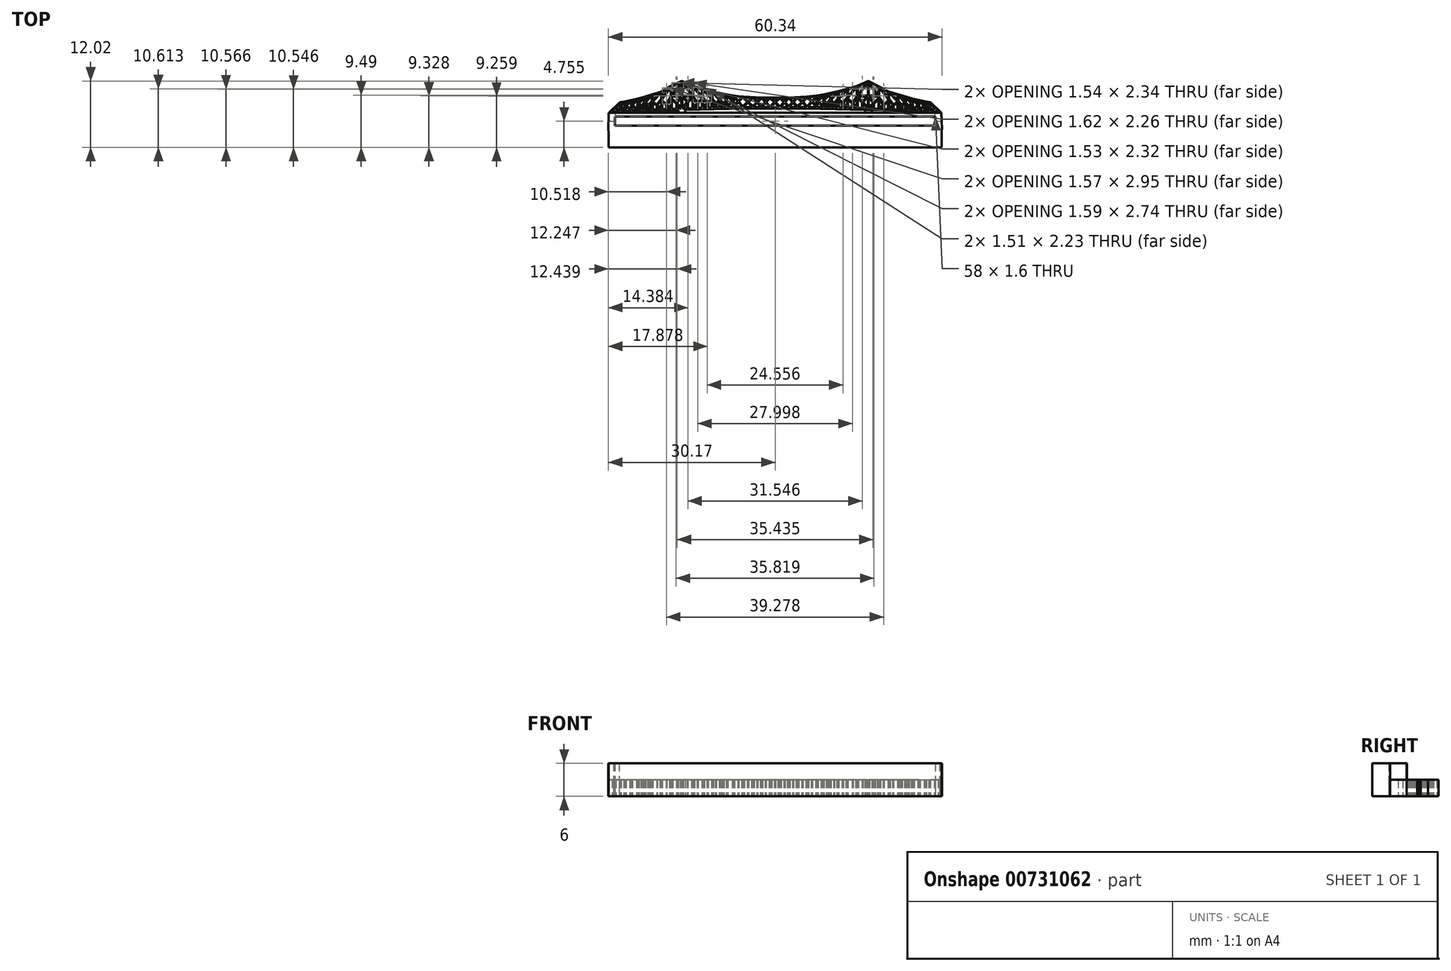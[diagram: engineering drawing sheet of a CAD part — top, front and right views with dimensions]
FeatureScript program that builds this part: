
annotation { "Feature Type Name" : "Feature", "Feature Type Description" : "" }
export const myFeature = defineFeature(function(context is Context, id is Id, definition is map)
    precondition{}
    {
        {
            var Q0;
            Q0=qCreatedBy(makeId("Top.planeOp"),FACE);
            var sketch = newSketch(context, id + "F0", { "sketchPlane" : qUnion([Q0])});
            skLineSegment(sketch, "E0", {"start": v(-17.64, -5.59) * mm, "end": v(-16.17, -5.64) * mm});
            skLineSegment(sketch, "E1", {"start": v(-16.17, -5.64) * mm, "end": v(-16.3, 0.12) * mm});
            skLineSegment(sketch, "E2", {"start": v(-16.3, 0.12) * mm, "end": v(-17.5, 0) * mm});
            skLineSegment(sketch, "E3", {"start": v(-17.5, 0) * mm, "end": v(-17.64, -5.59) * mm});
            skLineSegment(sketch, "E4", {"start": v(-30.17, -3.73) * mm, "end": v(-28.85, -3.82) * mm});
            skLineSegment(sketch, "E5", {"start": v(-28.85, -3.82) * mm, "end": v(-28.91, -0.44) * mm});
            skLineSegment(sketch, "E6", {"start": v(-28.91, -0.44) * mm, "end": v(-30.11, -0.52) * mm});
            skLineSegment(sketch, "E7", {"start": v(-30.11, -0.52) * mm, "end": v(-30.17, -3.73) * mm});
            skLineSegment(sketch, "E8", {"start": v(17.53, -3.47) * mm, "end": v(16.2, -3.47) * mm});
            skLineSegment(sketch, "E9", {"start": v(16.2, -3.47) * mm, "end": v(16.26, 0.16) * mm});
            skLineSegment(sketch, "E10", {"start": v(16.26, 0.16) * mm, "end": v(17.47, 0.13) * mm});
            skLineSegment(sketch, "E11", {"start": v(17.47, 0.13) * mm, "end": v(17.53, -3.47) * mm});
            skLineSegment(sketch, "E12", {"start": v(28.81, -3.47) * mm, "end": v(30.17, -3.47) * mm});
            skLineSegment(sketch, "E13", {"start": v(30.17, -3.47) * mm, "end": v(30.1, -0.5) * mm});
            skLineSegment(sketch, "E14", {"start": v(30.1, -0.5) * mm, "end": v(28.9, -0.37) * mm});
            skLineSegment(sketch, "E15", {"start": v(28.9, -0.37) * mm, "end": v(28.81, -3.47) * mm});
            skLineSegment(sketch, "E16", {"start": v(-18.7, 2.63) * mm, "end": v(-18.7, 4.23) * mm});
            skLineSegment(sketch, "E17", {"start": v(-18.7, 4.23) * mm, "end": v(-17.15, 4.99) * mm});
            skLineSegment(sketch, "E18", {"start": v(-17.15, 4.99) * mm, "end": v(-18.7, 2.64) * mm});
            skLineSegment(sketch, "E19", {"start": v(-16.6, 5) * mm, "end": v(-14.98, 2.73) * mm});
            skLineSegment(sketch, "E20", {"start": v(-14.98, 2.73) * mm, "end": v(-14.98, 4.26) * mm});
            skLineSegment(sketch, "E21", {"start": v(-14.98, 4.26) * mm, "end": v(-16.6, 5) * mm});
            skLineSegment(sketch, "E22", {"start": v(-16.8, 2.38) * mm, "end": v(-16.8, 0.54) * mm});
            skLineSegment(sketch, "E23", {"start": v(-16.8, 0.54) * mm, "end": v(-15.95, 1.45) * mm});
            skLineSegment(sketch, "E24", {"start": v(-15.95, 1.45) * mm, "end": v(-16.8, 2.38) * mm});
            skLineSegment(sketch, "E25", {"start": v(-16.96, 2.35) * mm, "end": v(-16.96, 0.53) * mm});
            skLineSegment(sketch, "E26", {"start": v(-16.96, 0.53) * mm, "end": v(-17.74, 1.25) * mm});
            skLineSegment(sketch, "E27", {"start": v(-17.74, 1.25) * mm, "end": v(-16.96, 2.35) * mm});
            skLineSegment(sketch, "E28", {"start": v(-18.87, 2.07) * mm, "end": v(-18.87, 0.45) * mm});
            skLineSegment(sketch, "E29", {"start": v(-18.87, 0.45) * mm, "end": v(-19.57, 1) * mm});
            skLineSegment(sketch, "E30", {"start": v(-19.57, 1) * mm, "end": v(-18.87, 2.07) * mm});
            skLineSegment(sketch, "E31", {"start": v(-20.6, 1.8) * mm, "end": v(-20.6, 0.37) * mm});
            skLineSegment(sketch, "E32", {"start": v(-20.6, 0.37) * mm, "end": v(-21.3, 0.92) * mm});
            skLineSegment(sketch, "E33", {"start": v(-21.3, 0.92) * mm, "end": v(-20.6, 1.8) * mm});
            skLineSegment(sketch, "E34", {"start": v(-22.33, 1.4) * mm, "end": v(-22.33, 0.34) * mm});
            skLineSegment(sketch, "E35", {"start": v(-22.33, 0.34) * mm, "end": v(-22.86, 0.88) * mm});
            skLineSegment(sketch, "E36", {"start": v(-22.86, 0.88) * mm, "end": v(-22.33, 1.4) * mm});
            skLineSegment(sketch, "E37", {"start": v(-23.7, 1.14) * mm, "end": v(-23.7, 0.29) * mm});
            skLineSegment(sketch, "E38", {"start": v(-23.7, 0.29) * mm, "end": v(-24.12, 0.71) * mm});
            skLineSegment(sketch, "E39", {"start": v(-24.12, 0.71) * mm, "end": v(-23.7, 1.14) * mm});
            skLineSegment(sketch, "E40", {"start": v(-27.92, 0.89) * mm, "end": v(-27.92, 1.3) * mm});
            skLineSegment(sketch, "E41", {"start": v(-27.92, 1.3) * mm, "end": v(-27.43, 1.37) * mm});
            skLineSegment(sketch, "E42", {"start": v(-27.43, 1.37) * mm, "end": v(-27.92, 0.89) * mm});
            skLineSegment(sketch, "E43", {"start": v(-27.05, 0.87) * mm, "end": v(-27.05, 1.45) * mm});
            skLineSegment(sketch, "E44", {"start": v(-27.05, 1.45) * mm, "end": v(-26.3, 1.61) * mm});
            skLineSegment(sketch, "E45", {"start": v(-26.3, 1.61) * mm, "end": v(-27.05, 0.87) * mm});
            skLineSegment(sketch, "E46", {"start": v(-25.9, 1.7) * mm, "end": v(-25.9, 1.08) * mm});
            skLineSegment(sketch, "E47", {"start": v(-25.9, 1.08) * mm, "end": v(-25.15, 1.84) * mm});
            skLineSegment(sketch, "E48", {"start": v(-25.15, 1.84) * mm, "end": v(-25.9, 1.7) * mm});
            skLineSegment(sketch, "E49", {"start": v(-24.76, 1.92) * mm, "end": v(-24.76, 1.35) * mm});
            skLineSegment(sketch, "E50", {"start": v(-24.76, 1.35) * mm, "end": v(-23.96, 2.16) * mm});
            skLineSegment(sketch, "E51", {"start": v(-23.96, 2.16) * mm, "end": v(-24.76, 1.92) * mm});
            skLineSegment(sketch, "E52", {"start": v(-23.53, 1.57) * mm, "end": v(-23.53, 2.28) * mm});
            skLineSegment(sketch, "E53", {"start": v(-23.53, 2.28) * mm, "end": v(-22.57, 2.58) * mm});
            skLineSegment(sketch, "E54", {"start": v(-22.57, 2.58) * mm, "end": v(-23.53, 1.57) * mm});
            skLineSegment(sketch, "E55", {"start": v(-22.16, 1.82) * mm, "end": v(-22.16, 2.7) * mm});
            skLineSegment(sketch, "E56", {"start": v(-22.16, 2.7) * mm, "end": v(-20.87, 3.11) * mm});
            skLineSegment(sketch, "E57", {"start": v(-20.87, 3.11) * mm, "end": v(-22.16, 1.82) * mm});
            skLineSegment(sketch, "E58", {"start": v(-20.44, 2.3) * mm, "end": v(-20.44, 3.27) * mm});
            skLineSegment(sketch, "E59", {"start": v(-20.44, 3.27) * mm, "end": v(-19.13, 4) * mm});
            skLineSegment(sketch, "E60", {"start": v(-19.13, 4) * mm, "end": v(-20.44, 2.3) * mm});
            skLineSegment(sketch, "E61", {"start": v(-14.8, 2.2) * mm, "end": v(-14.13, 1.26) * mm});
            skLineSegment(sketch, "E62", {"start": v(-14.13, 1.26) * mm, "end": v(-14.8, 0.59) * mm});
            skLineSegment(sketch, "E63", {"start": v(-14.8, 0.59) * mm, "end": v(-14.8, 2.2) * mm});
            skLineSegment(sketch, "E64", {"start": v(-13.05, 2.06) * mm, "end": v(-13.05, 0.7) * mm});
            skLineSegment(sketch, "E65", {"start": v(-13.05, 0.7) * mm, "end": v(-12.37, 1.28) * mm});
            skLineSegment(sketch, "E66", {"start": v(-12.37, 1.28) * mm, "end": v(-13.05, 2.06) * mm});
            skLineSegment(sketch, "E67", {"start": v(-11.35, 1.8) * mm, "end": v(-11.35, 0.71) * mm});
            skLineSegment(sketch, "E68", {"start": v(-11.35, 0.71) * mm, "end": v(-10.81, 1.22) * mm});
            skLineSegment(sketch, "E69", {"start": v(-10.81, 1.22) * mm, "end": v(-11.35, 1.8) * mm});
            skLineSegment(sketch, "E70", {"start": v(-13.22, 2.53) * mm, "end": v(-13.22, 3.75) * mm});
            skLineSegment(sketch, "E71", {"start": v(-13.22, 3.75) * mm, "end": v(-14.6, 4.14) * mm});
            skLineSegment(sketch, "E72", {"start": v(-14.6, 4.14) * mm, "end": v(-13.22, 2.53) * mm});
            skLineSegment(sketch, "E73", {"start": v(-11.53, 2.24) * mm, "end": v(-11.53, 3.25) * mm});
            skLineSegment(sketch, "E74", {"start": v(-11.53, 3.25) * mm, "end": v(-12.82, 3.63) * mm});
            skLineSegment(sketch, "E75", {"start": v(-12.82, 3.63) * mm, "end": v(-11.53, 2.24) * mm});
            skLineSegment(sketch, "E76", {"start": v(-10.12, 2.11) * mm, "end": v(-10.12, 2.95) * mm});
            skLineSegment(sketch, "E77", {"start": v(-10.12, 2.95) * mm, "end": v(-11.14, 3.16) * mm});
            skLineSegment(sketch, "E78", {"start": v(-11.14, 3.16) * mm, "end": v(-10.12, 2.11) * mm});
            skLineSegment(sketch, "E79", {"start": v(-8.9, 2.03) * mm, "end": v(-8.9, 2.7) * mm});
            skLineSegment(sketch, "E80", {"start": v(-8.9, 2.7) * mm, "end": v(-9.73, 2.87) * mm});
            skLineSegment(sketch, "E81", {"start": v(-9.73, 2.87) * mm, "end": v(-8.9, 2.03) * mm});
            skLineSegment(sketch, "E82", {"start": v(-7.66, 1.77) * mm, "end": v(-7.66, 2.51) * mm});
            skLineSegment(sketch, "E83", {"start": v(-7.66, 2.51) * mm, "end": v(-8.52, 2.64) * mm});
            skLineSegment(sketch, "E84", {"start": v(-8.52, 2.64) * mm, "end": v(-7.66, 1.77) * mm});
            skLineSegment(sketch, "E85", {"start": v(-9.95, 1.7) * mm, "end": v(-9.95, 0.75) * mm});
            skLineSegment(sketch, "E86", {"start": v(-9.95, 0.75) * mm, "end": v(-9.48, 1.21) * mm});
            skLineSegment(sketch, "E87", {"start": v(-9.48, 1.21) * mm, "end": v(-9.95, 1.7) * mm});
            skLineSegment(sketch, "E88", {"start": v(-7.5, 0.53) * mm, "end": v(-6.67, 1.4) * mm});
            skLineSegment(sketch, "E89", {"start": v(-6.67, 1.4) * mm, "end": v(-5.94, 0.53) * mm});
            skLineSegment(sketch, "E90", {"start": v(-5.94, 0.53) * mm, "end": v(-7.5, 0.53) * mm});
            skLineSegment(sketch, "E91", {"start": v(-5.77, 0.52) * mm, "end": v(-4.94, 1.36) * mm});
            skLineSegment(sketch, "E92", {"start": v(-4.94, 1.36) * mm, "end": v(-4.14, 0.55) * mm});
            skLineSegment(sketch, "E93", {"start": v(-4.14, 0.55) * mm, "end": v(-5.77, 0.53) * mm});
            skLineSegment(sketch, "E94", {"start": v(-3.97, 0.55) * mm, "end": v(-3.25, 1.3) * mm});
            skLineSegment(sketch, "E95", {"start": v(-3.25, 1.3) * mm, "end": v(-2.58, 0.55) * mm});
            skLineSegment(sketch, "E96", {"start": v(-2.58, 0.55) * mm, "end": v(-3.97, 0.55) * mm});
            skLineSegment(sketch, "E97", {"start": v(-1.7, 1.3) * mm, "end": v(-2.4, 0.55) * mm});
            skLineSegment(sketch, "E98", {"start": v(-2.4, 0.55) * mm, "end": v(-0.98, 0.55) * mm});
            skLineSegment(sketch, "E99", {"start": v(-0.98, 0.55) * mm, "end": v(-1.7, 1.3) * mm});
            skLineSegment(sketch, "E100", {"start": v(-1.7, 1.54) * mm, "end": v(-1.15, 2.1) * mm});
            skLineSegment(sketch, "E101", {"start": v(-1.15, 2.1) * mm, "end": v(-2.24, 2.1) * mm});
            skLineSegment(sketch, "E102", {"start": v(-2.24, 2.1) * mm, "end": v(-1.7, 1.54) * mm});
            skLineSegment(sketch, "E103", {"start": v(-2.72, 2.12) * mm, "end": v(-3.8, 2.18) * mm});
            skLineSegment(sketch, "E104", {"start": v(-3.8, 2.18) * mm, "end": v(-3.25, 1.56) * mm});
            skLineSegment(sketch, "E105", {"start": v(-3.25, 1.56) * mm, "end": v(-2.72, 2.12) * mm});
            skLineSegment(sketch, "E106", {"start": v(-4.3, 2.2) * mm, "end": v(-4.92, 1.6) * mm});
            skLineSegment(sketch, "E107", {"start": v(-4.92, 1.6) * mm, "end": v(-5.59, 2.27) * mm});
            skLineSegment(sketch, "E108", {"start": v(-5.59, 2.27) * mm, "end": v(-4.3, 2.2) * mm});
            skLineSegment(sketch, "E109", {"start": v(-7.33, 2.47) * mm, "end": v(-6.66, 1.67) * mm});
            skLineSegment(sketch, "E110", {"start": v(-6.66, 1.67) * mm, "end": v(-6.07, 2.31) * mm});
            skLineSegment(sketch, "E111", {"start": v(-6.07, 2.31) * mm, "end": v(-7.33, 2.47) * mm});
            skLineSegment(sketch, "E112", {"start": v(18.67, 2.63) * mm, "end": v(18.67, 4.23) * mm});
            skLineSegment(sketch, "E113", {"start": v(18.67, 4.23) * mm, "end": v(17.12, 4.99) * mm});
            skLineSegment(sketch, "E114", {"start": v(17.12, 4.99) * mm, "end": v(18.67, 2.64) * mm});
            skLineSegment(sketch, "E115", {"start": v(16.57, 5) * mm, "end": v(14.95, 2.73) * mm});
            skLineSegment(sketch, "E116", {"start": v(14.95, 2.73) * mm, "end": v(14.95, 4.26) * mm});
            skLineSegment(sketch, "E117", {"start": v(14.95, 4.26) * mm, "end": v(16.57, 5) * mm});
            skLineSegment(sketch, "E118", {"start": v(16.77, 2.38) * mm, "end": v(16.77, 0.54) * mm});
            skLineSegment(sketch, "E119", {"start": v(16.77, 0.54) * mm, "end": v(15.92, 1.45) * mm});
            skLineSegment(sketch, "E120", {"start": v(15.92, 1.45) * mm, "end": v(16.77, 2.38) * mm});
            skLineSegment(sketch, "E121", {"start": v(16.94, 2.35) * mm, "end": v(16.94, 0.53) * mm});
            skLineSegment(sketch, "E122", {"start": v(16.94, 0.53) * mm, "end": v(17.71, 1.25) * mm});
            skLineSegment(sketch, "E123", {"start": v(17.71, 1.25) * mm, "end": v(16.94, 2.35) * mm});
            skLineSegment(sketch, "E124", {"start": v(18.84, 2.07) * mm, "end": v(18.84, 0.45) * mm});
            skLineSegment(sketch, "E125", {"start": v(18.84, 0.45) * mm, "end": v(19.54, 1) * mm});
            skLineSegment(sketch, "E126", {"start": v(19.54, 1) * mm, "end": v(18.84, 2.07) * mm});
            skLineSegment(sketch, "E127", {"start": v(20.58, 1.8) * mm, "end": v(20.58, 0.37) * mm});
            skLineSegment(sketch, "E128", {"start": v(20.58, 0.37) * mm, "end": v(21.26, 0.92) * mm});
            skLineSegment(sketch, "E129", {"start": v(21.26, 0.92) * mm, "end": v(20.58, 1.8) * mm});
            skLineSegment(sketch, "E130", {"start": v(22.3, 1.4) * mm, "end": v(22.3, 0.34) * mm});
            skLineSegment(sketch, "E131", {"start": v(22.3, 0.34) * mm, "end": v(22.84, 0.88) * mm});
            skLineSegment(sketch, "E132", {"start": v(22.84, 0.88) * mm, "end": v(22.3, 1.4) * mm});
            skLineSegment(sketch, "E133", {"start": v(23.68, 1.14) * mm, "end": v(23.68, 0.29) * mm});
            skLineSegment(sketch, "E134", {"start": v(23.68, 0.29) * mm, "end": v(24.1, 0.71) * mm});
            skLineSegment(sketch, "E135", {"start": v(24.1, 0.71) * mm, "end": v(23.68, 1.14) * mm});
            skLineSegment(sketch, "E136", {"start": v(27.9, 0.89) * mm, "end": v(27.9, 1.3) * mm});
            skLineSegment(sketch, "E137", {"start": v(27.9, 1.3) * mm, "end": v(27.4, 1.37) * mm});
            skLineSegment(sketch, "E138", {"start": v(27.4, 1.37) * mm, "end": v(27.9, 0.89) * mm});
            skLineSegment(sketch, "E139", {"start": v(27.02, 0.87) * mm, "end": v(27.02, 1.45) * mm});
            skLineSegment(sketch, "E140", {"start": v(27.02, 1.45) * mm, "end": v(26.28, 1.61) * mm});
            skLineSegment(sketch, "E141", {"start": v(26.28, 1.61) * mm, "end": v(27.02, 0.87) * mm});
            skLineSegment(sketch, "E142", {"start": v(25.88, 1.7) * mm, "end": v(25.88, 1.08) * mm});
            skLineSegment(sketch, "E143", {"start": v(25.88, 1.08) * mm, "end": v(25.12, 1.84) * mm});
            skLineSegment(sketch, "E144", {"start": v(25.12, 1.84) * mm, "end": v(25.88, 1.7) * mm});
            skLineSegment(sketch, "E145", {"start": v(24.73, 1.92) * mm, "end": v(24.73, 1.35) * mm});
            skLineSegment(sketch, "E146", {"start": v(24.73, 1.35) * mm, "end": v(23.93, 2.16) * mm});
            skLineSegment(sketch, "E147", {"start": v(23.93, 2.16) * mm, "end": v(24.73, 1.92) * mm});
            skLineSegment(sketch, "E148", {"start": v(23.5, 1.57) * mm, "end": v(23.5, 2.28) * mm});
            skLineSegment(sketch, "E149", {"start": v(23.5, 2.28) * mm, "end": v(22.55, 2.58) * mm});
            skLineSegment(sketch, "E150", {"start": v(22.55, 2.58) * mm, "end": v(23.5, 1.57) * mm});
            skLineSegment(sketch, "E151", {"start": v(22.13, 1.82) * mm, "end": v(22.13, 2.7) * mm});
            skLineSegment(sketch, "E152", {"start": v(22.13, 2.7) * mm, "end": v(20.85, 3.11) * mm});
            skLineSegment(sketch, "E153", {"start": v(20.85, 3.11) * mm, "end": v(22.13, 1.82) * mm});
            skLineSegment(sketch, "E154", {"start": v(20.41, 2.3) * mm, "end": v(20.41, 3.27) * mm});
            skLineSegment(sketch, "E155", {"start": v(20.41, 3.27) * mm, "end": v(19.1, 4) * mm});
            skLineSegment(sketch, "E156", {"start": v(19.1, 4) * mm, "end": v(20.41, 2.3) * mm});
            skLineSegment(sketch, "E157", {"start": v(14.78, 2.2) * mm, "end": v(14.1, 1.26) * mm});
            skLineSegment(sketch, "E158", {"start": v(14.1, 1.26) * mm, "end": v(14.78, 0.59) * mm});
            skLineSegment(sketch, "E159", {"start": v(14.78, 0.59) * mm, "end": v(14.78, 2.2) * mm});
            skLineSegment(sketch, "E160", {"start": v(13.02, 2.06) * mm, "end": v(13.02, 0.7) * mm});
            skLineSegment(sketch, "E161", {"start": v(13.02, 0.7) * mm, "end": v(12.35, 1.28) * mm});
            skLineSegment(sketch, "E162", {"start": v(12.35, 1.28) * mm, "end": v(13.02, 2.06) * mm});
            skLineSegment(sketch, "E163", {"start": v(11.33, 1.8) * mm, "end": v(11.33, 0.71) * mm});
            skLineSegment(sketch, "E164", {"start": v(11.33, 0.71) * mm, "end": v(10.78, 1.22) * mm});
            skLineSegment(sketch, "E165", {"start": v(10.78, 1.22) * mm, "end": v(11.33, 1.8) * mm});
            skLineSegment(sketch, "E166", {"start": v(13.2, 2.53) * mm, "end": v(13.2, 3.75) * mm});
            skLineSegment(sketch, "E167", {"start": v(13.2, 3.75) * mm, "end": v(14.58, 4.14) * mm});
            skLineSegment(sketch, "E168", {"start": v(14.58, 4.14) * mm, "end": v(13.2, 2.53) * mm});
            skLineSegment(sketch, "E169", {"start": v(11.5, 2.24) * mm, "end": v(11.5, 3.25) * mm});
            skLineSegment(sketch, "E170", {"start": v(11.5, 3.25) * mm, "end": v(12.8, 3.63) * mm});
            skLineSegment(sketch, "E171", {"start": v(12.8, 3.63) * mm, "end": v(11.5, 2.24) * mm});
            skLineSegment(sketch, "E172", {"start": v(10.1, 2.11) * mm, "end": v(10.1, 2.95) * mm});
            skLineSegment(sketch, "E173", {"start": v(10.1, 2.95) * mm, "end": v(11.11, 3.16) * mm});
            skLineSegment(sketch, "E174", {"start": v(11.11, 3.16) * mm, "end": v(10.1, 2.11) * mm});
            skLineSegment(sketch, "E175", {"start": v(8.87, 2.03) * mm, "end": v(8.87, 2.7) * mm});
            skLineSegment(sketch, "E176", {"start": v(8.87, 2.7) * mm, "end": v(9.7, 2.87) * mm});
            skLineSegment(sketch, "E177", {"start": v(9.7, 2.87) * mm, "end": v(8.87, 2.03) * mm});
            skLineSegment(sketch, "E178", {"start": v(7.64, 1.77) * mm, "end": v(7.64, 2.51) * mm});
            skLineSegment(sketch, "E179", {"start": v(7.64, 2.51) * mm, "end": v(8.5, 2.64) * mm});
            skLineSegment(sketch, "E180", {"start": v(8.5, 2.64) * mm, "end": v(7.64, 1.77) * mm});
            skLineSegment(sketch, "E181", {"start": v(9.92, 1.7) * mm, "end": v(9.92, 0.75) * mm});
            skLineSegment(sketch, "E182", {"start": v(9.92, 0.75) * mm, "end": v(9.45, 1.21) * mm});
            skLineSegment(sketch, "E183", {"start": v(9.45, 1.21) * mm, "end": v(9.92, 1.7) * mm});
            skLineSegment(sketch, "E184", {"start": v(7.46, 0.53) * mm, "end": v(6.64, 1.4) * mm});
            skLineSegment(sketch, "E185", {"start": v(6.64, 1.4) * mm, "end": v(5.91, 0.53) * mm});
            skLineSegment(sketch, "E186", {"start": v(5.91, 0.53) * mm, "end": v(7.46, 0.53) * mm});
            skLineSegment(sketch, "E187", {"start": v(5.74, 0.53) * mm, "end": v(4.9, 1.36) * mm});
            skLineSegment(sketch, "E188", {"start": v(4.9, 1.36) * mm, "end": v(4.11, 0.55) * mm});
            skLineSegment(sketch, "E189", {"start": v(4.11, 0.55) * mm, "end": v(5.74, 0.53) * mm});
            skLineSegment(sketch, "E190", {"start": v(3.94, 0.55) * mm, "end": v(3.23, 1.3) * mm});
            skLineSegment(sketch, "E191", {"start": v(3.23, 1.3) * mm, "end": v(2.55, 0.55) * mm});
            skLineSegment(sketch, "E192", {"start": v(2.55, 0.55) * mm, "end": v(3.94, 0.55) * mm});
            skLineSegment(sketch, "E193", {"start": v(1.67, 1.3) * mm, "end": v(2.38, 0.55) * mm});
            skLineSegment(sketch, "E194", {"start": v(2.38, 0.55) * mm, "end": v(0.95, 0.55) * mm});
            skLineSegment(sketch, "E195", {"start": v(0.95, 0.55) * mm, "end": v(1.67, 1.3) * mm});
            skLineSegment(sketch, "E196", {"start": v(1.67, 1.54) * mm, "end": v(1.12, 2.1) * mm});
            skLineSegment(sketch, "E197", {"start": v(1.12, 2.1) * mm, "end": v(2.21, 2.1) * mm});
            skLineSegment(sketch, "E198", {"start": v(2.21, 2.1) * mm, "end": v(1.67, 1.54) * mm});
            skLineSegment(sketch, "E199", {"start": v(2.7, 2.12) * mm, "end": v(3.78, 2.18) * mm});
            skLineSegment(sketch, "E200", {"start": v(3.78, 2.18) * mm, "end": v(3.22, 1.56) * mm});
            skLineSegment(sketch, "E201", {"start": v(3.22, 1.56) * mm, "end": v(2.7, 2.12) * mm});
            skLineSegment(sketch, "E202", {"start": v(4.27, 2.2) * mm, "end": v(4.9, 1.6) * mm});
            skLineSegment(sketch, "E203", {"start": v(4.9, 1.6) * mm, "end": v(5.56, 2.27) * mm});
            skLineSegment(sketch, "E204", {"start": v(5.56, 2.27) * mm, "end": v(4.27, 2.2) * mm});
            skLineSegment(sketch, "E205", {"start": v(7.3, 2.47) * mm, "end": v(6.64, 1.67) * mm});
            skLineSegment(sketch, "E206", {"start": v(6.64, 1.67) * mm, "end": v(6.04, 2.31) * mm});
            skLineSegment(sketch, "E207", {"start": v(6.04, 2.31) * mm, "end": v(7.3, 2.47) * mm});
            skLineSegment(sketch, "E208", {"start": v(-0.05, 1.29) * mm, "end": v(-0.76, 0.55) * mm});
            skLineSegment(sketch, "E209", {"start": v(-0.76, 0.55) * mm, "end": v(0.67, 0.54) * mm});
            skLineSegment(sketch, "E210", {"start": v(0.67, 0.54) * mm, "end": v(-0.05, 1.29) * mm});
            skLineSegment(sketch, "E211", {"start": v(-0.05, 1.53) * mm, "end": v(0.5, 2.1) * mm});
            skLineSegment(sketch, "E212", {"start": v(0.5, 2.1) * mm, "end": v(-0.6, 2.1) * mm});
            skLineSegment(sketch, "E213", {"start": v(-0.6, 2.1) * mm, "end": v(-0.05, 1.53) * mm});
            skLineSegment(sketch, "E214", {"start": v(18.84, 4.05) * mm, "end": v(20.41, 2.02) * mm});
            skLineSegment(sketch, "E215", {"start": v(20.41, 2.02) * mm, "end": v(20.41, 1.7) * mm});
            skLineSegment(sketch, "E216", {"start": v(20.41, 1.7) * mm, "end": v(19.71, 1.1) * mm});
            skLineSegment(sketch, "E217", {"start": v(19.71, 1.1) * mm, "end": v(18.84, 2.38) * mm});
            skLineSegment(sketch, "E218", {"start": v(18.84, 2.38) * mm, "end": v(18.84, 4.05) * mm});
            skLineSegment(sketch, "E219", {"start": v(16.94, 4.96) * mm, "end": v(16.94, 2.64) * mm});
            skLineSegment(sketch, "E220", {"start": v(16.94, 2.64) * mm, "end": v(18.47, 2.63) * mm});
            skLineSegment(sketch, "E221", {"start": v(18.47, 2.63) * mm, "end": v(16.94, 4.96) * mm});
            skLineSegment(sketch, "E222", {"start": v(17.05, 2.48) * mm, "end": v(18.58, 2.46) * mm});
            skLineSegment(sketch, "E223", {"start": v(18.58, 2.46) * mm, "end": v(18.67, 2.33) * mm});
            skLineSegment(sketch, "E224", {"start": v(18.67, 2.33) * mm, "end": v(18.71, 2.19) * mm});
            skLineSegment(sketch, "E225", {"start": v(18.71, 2.19) * mm, "end": v(17.84, 1.37) * mm});
            skLineSegment(sketch, "E226", {"start": v(17.84, 1.37) * mm, "end": v(17.05, 2.48) * mm});
            skLineSegment(sketch, "E227", {"start": v(18.67, 0.23) * mm, "end": v(18.67, 1.91) * mm});
            skLineSegment(sketch, "E228", {"start": v(18.67, 1.91) * mm, "end": v(17.88, 1.17) * mm});
            skLineSegment(sketch, "E229", {"start": v(17.88, 1.17) * mm, "end": v(17.88, 0.27) * mm});
            skLineSegment(sketch, "E230", {"start": v(17.88, 0.27) * mm, "end": v(18.67, 0.23) * mm});
            skLineSegment(sketch, "E231", {"start": v(20.41, 0.15) * mm, "end": v(20.41, 1.47) * mm});
            skLineSegment(sketch, "E232", {"start": v(20.41, 1.47) * mm, "end": v(19.71, 0.92) * mm});
            skLineSegment(sketch, "E233", {"start": v(19.71, 0.92) * mm, "end": v(19.71, 0.2) * mm});
            skLineSegment(sketch, "E234", {"start": v(19.71, 0.2) * mm, "end": v(20.41, 0.15) * mm});
            skLineSegment(sketch, "E235", {"start": v(19.54, 0.78) * mm, "end": v(19.54, 0.2) * mm});
            skLineSegment(sketch, "E236", {"start": v(19.54, 0.2) * mm, "end": v(18.84, 0.23) * mm});
            skLineSegment(sketch, "E237", {"start": v(18.84, 0.23) * mm, "end": v(19.54, 0.78) * mm});
            skLineSegment(sketch, "E238", {"start": v(20.58, 3.13) * mm, "end": v(22.12, 1.6) * mm});
            skLineSegment(sketch, "E239", {"start": v(22.12, 1.6) * mm, "end": v(21.4, 1.02) * mm});
            skLineSegment(sketch, "E240", {"start": v(21.4, 1.02) * mm, "end": v(20.58, 2.08) * mm});
            skLineSegment(sketch, "E241", {"start": v(20.58, 2.08) * mm, "end": v(20.58, 3.13) * mm});
            skLineSegment(sketch, "E242", {"start": v(22.13, 1.39) * mm, "end": v(22.13, 0.1) * mm});
            skLineSegment(sketch, "E243", {"start": v(22.13, 0.1) * mm, "end": v(21.44, 0.1) * mm});
            skLineSegment(sketch, "E244", {"start": v(21.44, 0.1) * mm, "end": v(21.44, 0.83) * mm});
            skLineSegment(sketch, "E245", {"start": v(21.44, 0.83) * mm, "end": v(22.13, 1.39) * mm});
            skLineSegment(sketch, "E246", {"start": v(21.27, 0.7) * mm, "end": v(21.27, 0.1) * mm});
            skLineSegment(sketch, "E247", {"start": v(21.27, 0.1) * mm, "end": v(20.58, 0.15) * mm});
            skLineSegment(sketch, "E248", {"start": v(20.58, 0.15) * mm, "end": v(21.27, 0.7) * mm});
            skLineSegment(sketch, "E249", {"start": v(17.7, 1.01) * mm, "end": v(17.7, 0.27) * mm});
            skLineSegment(sketch, "E250", {"start": v(17.7, 0.27) * mm, "end": v(16.94, 0.3) * mm});
            skLineSegment(sketch, "E251", {"start": v(16.94, 0.3) * mm, "end": v(17.7, 1.01) * mm});
            skLineSegment(sketch, "E252", {"start": v(26.05, 1.6) * mm, "end": v(26.92, 0.73) * mm});
            skLineSegment(sketch, "E253", {"start": v(26.92, 0.73) * mm, "end": v(26.05, 0.16) * mm});
            skLineSegment(sketch, "E254", {"start": v(26.05, 0.16) * mm, "end": v(26.05, 1.6) * mm});
            skLineSegment(sketch, "E255", {"start": v(24.9, 1.81) * mm, "end": v(25.79, 0.93) * mm});
            skLineSegment(sketch, "E256", {"start": v(25.79, 0.93) * mm, "end": v(24.9, 0.21) * mm});
            skLineSegment(sketch, "E257", {"start": v(24.9, 0.21) * mm, "end": v(24.9, 1.81) * mm});
            skLineSegment(sketch, "E258", {"start": v(23.68, 2.17) * mm, "end": v(24.6, 1.24) * mm});
            skLineSegment(sketch, "E259", {"start": v(24.6, 1.24) * mm, "end": v(24.21, 0.83) * mm});
            skLineSegment(sketch, "E260", {"start": v(24.21, 0.83) * mm, "end": v(23.68, 1.4) * mm});
            skLineSegment(sketch, "E261", {"start": v(23.68, 1.4) * mm, "end": v(23.68, 2.17) * mm});
            skLineSegment(sketch, "E262", {"start": v(23.5, 1.32) * mm, "end": v(23.5, 0.04) * mm});
            skLineSegment(sketch, "E263", {"start": v(23.5, 0.04) * mm, "end": v(23.03, 0.07) * mm});
            skLineSegment(sketch, "E264", {"start": v(23.03, 0.07) * mm, "end": v(23.03, 0.83) * mm});
            skLineSegment(sketch, "E265", {"start": v(23.03, 0.83) * mm, "end": v(23.5, 1.32) * mm});
            skLineSegment(sketch, "E266", {"start": v(23.39, 1.44) * mm, "end": v(22.96, 1) * mm});
            skLineSegment(sketch, "E267", {"start": v(22.96, 1) * mm, "end": v(22.3, 1.65) * mm});
            skLineSegment(sketch, "E268", {"start": v(22.3, 1.65) * mm, "end": v(22.3, 2.58) * mm});
            skLineSegment(sketch, "E269", {"start": v(22.3, 2.58) * mm, "end": v(23.39, 1.44) * mm});
            skLineSegment(sketch, "E270", {"start": v(22.86, 0.66) * mm, "end": v(22.86, 0.07) * mm});
            skLineSegment(sketch, "E271", {"start": v(22.86, 0.07) * mm, "end": v(22.3, 0.1) * mm});
            skLineSegment(sketch, "E272", {"start": v(22.3, 0.1) * mm, "end": v(22.86, 0.66) * mm});
            skLineSegment(sketch, "E273", {"start": v(24.73, -0.01) * mm, "end": v(24.73, 1.12) * mm});
            skLineSegment(sketch, "E274", {"start": v(24.73, 1.12) * mm, "end": v(24.27, 0.65) * mm});
            skLineSegment(sketch, "E275", {"start": v(24.27, 0.65) * mm, "end": v(24.27, 0.01) * mm});
            skLineSegment(sketch, "E276", {"start": v(24.27, 0.01) * mm, "end": v(24.73, -0.01) * mm});
            skLineSegment(sketch, "E277", {"start": v(24.1, 0.47) * mm, "end": v(24.1, 0.01) * mm});
            skLineSegment(sketch, "E278", {"start": v(24.1, 0.01) * mm, "end": v(23.68, 0.04) * mm});
            skLineSegment(sketch, "E279", {"start": v(23.68, 0.04) * mm, "end": v(24.1, 0.47) * mm});
            skLineSegment(sketch, "E280", {"start": v(25.88, 0.78) * mm, "end": v(25.88, -0.04) * mm});
            skLineSegment(sketch, "E281", {"start": v(25.88, -0.04) * mm, "end": v(24.9, -0.01) * mm});
            skLineSegment(sketch, "E282", {"start": v(24.9, -0.01) * mm, "end": v(25.88, 0.78) * mm});
            skLineSegment(sketch, "E283", {"start": v(27.02, 0.6) * mm, "end": v(27.02, -0.14) * mm});
            skLineSegment(sketch, "E284", {"start": v(27.02, -0.14) * mm, "end": v(26.05, -0.04) * mm});
            skLineSegment(sketch, "E285", {"start": v(26.05, -0.04) * mm, "end": v(27.02, 0.6) * mm});
            skLineSegment(sketch, "E286", {"start": v(27.2, 1.34) * mm, "end": v(27.81, 0.72) * mm});
            skLineSegment(sketch, "E287", {"start": v(27.81, 0.72) * mm, "end": v(27.2, 0.1) * mm});
            skLineSegment(sketch, "E288", {"start": v(27.2, 0.1) * mm, "end": v(27.2, 1.34) * mm});
            skLineSegment(sketch, "E289", {"start": v(27.9, 0.56) * mm, "end": v(27.9, -0.17) * mm});
            skLineSegment(sketch, "E290", {"start": v(27.9, -0.17) * mm, "end": v(27.2, -0.14) * mm});
            skLineSegment(sketch, "E291", {"start": v(27.2, -0.14) * mm, "end": v(27.9, 0.56) * mm});
            skLineSegment(sketch, "E292", {"start": v(28.06, 0.03) * mm, "end": v(28.06, 1.2) * mm});
            skLineSegment(sketch, "E293", {"start": v(28.06, 1.2) * mm, "end": v(28.8, 0.45) * mm});
            skLineSegment(sketch, "E294", {"start": v(28.8, 0.45) * mm, "end": v(28.06, 0.03) * mm});
            skLineSegment(sketch, "E295", {"start": v(28.93, 0.33) * mm, "end": v(29.5, -0.24) * mm});
            skLineSegment(sketch, "E296", {"start": v(29.5, -0.24) * mm, "end": v(28.06, -0.17) * mm});
            skLineSegment(sketch, "E297", {"start": v(28.06, -0.17) * mm, "end": v(28.93, 0.33) * mm});
            skLineSegment(sketch, "E298", {"start": v(6.53, 1.54) * mm, "end": v(5.83, 2.29) * mm});
            skLineSegment(sketch, "E299", {"start": v(5.83, 2.29) * mm, "end": v(5.02, 1.47) * mm});
            skLineSegment(sketch, "E300", {"start": v(5.02, 1.47) * mm, "end": v(5.82, 0.69) * mm});
            skLineSegment(sketch, "E301", {"start": v(5.82, 0.69) * mm, "end": v(6.53, 1.54) * mm});
            skLineSegment(sketch, "E302", {"start": v(4.78, 1.47) * mm, "end": v(4.04, 2.2) * mm});
            skLineSegment(sketch, "E303", {"start": v(4.04, 2.2) * mm, "end": v(3.34, 1.44) * mm});
            skLineSegment(sketch, "E304", {"start": v(3.34, 1.44) * mm, "end": v(4.03, 0.71) * mm});
            skLineSegment(sketch, "E305", {"start": v(4.03, 0.71) * mm, "end": v(4.78, 1.47) * mm});
            skLineSegment(sketch, "E306", {"start": v(2.45, 2.1) * mm, "end": v(3.1, 1.43) * mm});
            skLineSegment(sketch, "E307", {"start": v(3.1, 1.43) * mm, "end": v(2.46, 0.7) * mm});
            skLineSegment(sketch, "E308", {"start": v(2.46, 0.7) * mm, "end": v(1.78, 1.41) * mm});
            skLineSegment(sketch, "E309", {"start": v(1.78, 1.41) * mm, "end": v(2.45, 2.1) * mm});
            skLineSegment(sketch, "E310", {"start": v(0.83, 2.16) * mm, "end": v(1.54, 1.42) * mm});
            skLineSegment(sketch, "E311", {"start": v(1.54, 1.42) * mm, "end": v(0.83, 0.68) * mm});
            skLineSegment(sketch, "E312", {"start": v(0.83, 0.68) * mm, "end": v(0.07, 1.42) * mm});
            skLineSegment(sketch, "E313", {"start": v(0.08, 1.41) * mm, "end": v(0.83, 2.16) * mm});
            skLineSegment(sketch, "E314", {"start": v(-6.55, 1.54) * mm, "end": v(-5.86, 2.29) * mm});
            skLineSegment(sketch, "E315", {"start": v(-5.86, 2.29) * mm, "end": v(-5.04, 1.47) * mm});
            skLineSegment(sketch, "E316", {"start": v(-5.04, 1.47) * mm, "end": v(-5.85, 0.69) * mm});
            skLineSegment(sketch, "E317", {"start": v(-5.85, 0.69) * mm, "end": v(-6.55, 1.54) * mm});
            skLineSegment(sketch, "E318", {"start": v(-4.8, 1.47) * mm, "end": v(-4.06, 2.2) * mm});
            skLineSegment(sketch, "E319", {"start": v(-4.06, 2.2) * mm, "end": v(-3.37, 1.44) * mm});
            skLineSegment(sketch, "E320", {"start": v(-3.37, 1.44) * mm, "end": v(-4.06, 0.71) * mm});
            skLineSegment(sketch, "E321", {"start": v(-4.06, 0.71) * mm, "end": v(-4.8, 1.47) * mm});
            skLineSegment(sketch, "E322", {"start": v(-2.48, 2.1) * mm, "end": v(-3.14, 1.43) * mm});
            skLineSegment(sketch, "E323", {"start": v(-3.14, 1.43) * mm, "end": v(-2.49, 0.7) * mm});
            skLineSegment(sketch, "E324", {"start": v(-2.49, 0.7) * mm, "end": v(-1.81, 1.41) * mm});
            skLineSegment(sketch, "E325", {"start": v(-1.81, 1.41) * mm, "end": v(-2.48, 2.1) * mm});
            skLineSegment(sketch, "E326", {"start": v(-0.93, 2.15) * mm, "end": v(-1.64, 1.41) * mm});
            skLineSegment(sketch, "E327", {"start": v(-1.64, 1.41) * mm, "end": v(-0.93, 0.67) * mm});
            skLineSegment(sketch, "E328", {"start": v(-0.93, 0.67) * mm, "end": v(-0.17, 1.41) * mm});
            skLineSegment(sketch, "E329", {"start": v(-0.17, 1.4) * mm, "end": v(-0.93, 2.15) * mm});
            skLineSegment(sketch, "E330", {"start": v(16.77, 4.97) * mm, "end": v(16.77, 2.63) * mm});
            skLineSegment(sketch, "E331", {"start": v(16.77, 2.63) * mm, "end": v(15.1, 2.65) * mm});
            skLineSegment(sketch, "E332", {"start": v(15.1, 2.65) * mm, "end": v(16.77, 4.97) * mm});
            skLineSegment(sketch, "E333", {"start": v(16.61, 2.46) * mm, "end": v(15.8, 1.57) * mm});
            skLineSegment(sketch, "E334", {"start": v(15.8, 1.57) * mm, "end": v(14.97, 2.46) * mm});
            skLineSegment(sketch, "E335", {"start": v(14.97, 2.46) * mm, "end": v(14.98, 2.48) * mm});
            skLineSegment(sketch, "E336", {"start": v(14.98, 2.48) * mm, "end": v(16.61, 2.46) * mm});
            skLineSegment(sketch, "E337", {"start": v(14.78, 4.1) * mm, "end": v(14.78, 2.5) * mm});
            skLineSegment(sketch, "E338", {"start": v(14.78, 2.5) * mm, "end": v(13.98, 1.37) * mm});
            skLineSegment(sketch, "E339", {"start": v(13.98, 1.37) * mm, "end": v(13.2, 2.14) * mm});
            skLineSegment(sketch, "E340", {"start": v(13.2, 2.14) * mm, "end": v(13.2, 2.26) * mm});
            skLineSegment(sketch, "E341", {"start": v(13.2, 2.26) * mm, "end": v(14.78, 4.1) * mm});
            skLineSegment(sketch, "E342", {"start": v(13.93, 0.4) * mm, "end": v(13.93, 1.17) * mm});
            skLineSegment(sketch, "E343", {"start": v(13.93, 1.17) * mm, "end": v(13.2, 1.9) * mm});
            skLineSegment(sketch, "E344", {"start": v(13.2, 1.9) * mm, "end": v(13.2, 0.48) * mm});
            skLineSegment(sketch, "E345", {"start": v(13.2, 0.48) * mm, "end": v(13.93, 0.4) * mm});
            skLineSegment(sketch, "E346", {"start": v(14.95, 2.23) * mm, "end": v(15.73, 1.4) * mm});
            skLineSegment(sketch, "E347", {"start": v(15.73, 1.4) * mm, "end": v(15.73, 0.33) * mm});
            skLineSegment(sketch, "E348", {"start": v(15.73, 0.33) * mm, "end": v(14.95, 0.35) * mm});
            skLineSegment(sketch, "E349", {"start": v(14.95, 0.35) * mm, "end": v(14.95, 2.23) * mm});
            skLineSegment(sketch, "E350", {"start": v(15.9, 1.21) * mm, "end": v(16.77, 0.3) * mm});
            skLineSegment(sketch, "E351", {"start": v(16.77, 0.3) * mm, "end": v(15.9, 0.33) * mm});
            skLineSegment(sketch, "E352", {"start": v(15.9, 0.33) * mm, "end": v(15.9, 1.21) * mm});
            skLineSegment(sketch, "E353", {"start": v(14.1, 1) * mm, "end": v(14.78, 0.35) * mm});
            skLineSegment(sketch, "E354", {"start": v(14.78, 0.35) * mm, "end": v(14.1, 0.4) * mm});
            skLineSegment(sketch, "E355", {"start": v(14.1, 0.4) * mm, "end": v(14.1, 1) * mm});
            skLineSegment(sketch, "E356", {"start": v(13.02, 3.62) * mm, "end": v(13.02, 2.33) * mm});
            skLineSegment(sketch, "E357", {"start": v(13.02, 2.33) * mm, "end": v(12.22, 1.4) * mm});
            skLineSegment(sketch, "E358", {"start": v(12.22, 1.4) * mm, "end": v(11.5, 2) * mm});
            skLineSegment(sketch, "E359", {"start": v(11.5, 2) * mm, "end": v(13.02, 3.62) * mm});
            skLineSegment(sketch, "E360", {"start": v(11.33, 3.13) * mm, "end": v(11.33, 2.06) * mm});
            skLineSegment(sketch, "E361", {"start": v(11.33, 2.06) * mm, "end": v(10.66, 1.33) * mm});
            skLineSegment(sketch, "E362", {"start": v(10.66, 1.33) * mm, "end": v(10.1, 1.86) * mm});
            skLineSegment(sketch, "E363", {"start": v(10.1, 1.86) * mm, "end": v(11.33, 3.13) * mm});
            skLineSegment(sketch, "E364", {"start": v(11.5, 1.78) * mm, "end": v(12.1, 1.27) * mm});
            skLineSegment(sketch, "E365", {"start": v(12.1, 1.27) * mm, "end": v(12.1, 0.46) * mm});
            skLineSegment(sketch, "E366", {"start": v(12.1, 0.46) * mm, "end": v(11.5, 0.48) * mm});
            skLineSegment(sketch, "E367", {"start": v(11.5, 0.48) * mm, "end": v(11.5, 1.78) * mm});
            skLineSegment(sketch, "E368", {"start": v(12.27, 1.12) * mm, "end": v(13.02, 0.48) * mm});
            skLineSegment(sketch, "E369", {"start": v(13.02, 0.48) * mm, "end": v(12.27, 0.46) * mm});
            skLineSegment(sketch, "E370", {"start": v(12.27, 0.46) * mm, "end": v(12.27, 1.12) * mm});
            skLineSegment(sketch, "E371", {"start": v(11.33, 0.48) * mm, "end": v(10.76, 1) * mm});
            skLineSegment(sketch, "E372", {"start": v(10.76, 1) * mm, "end": v(10.76, 0.49) * mm});
            skLineSegment(sketch, "E373", {"start": v(10.76, 0.49) * mm, "end": v(11.33, 0.48) * mm});
            skLineSegment(sketch, "E374", {"start": v(10.6, 0.49) * mm, "end": v(10.1, 0.5) * mm});
            skLineSegment(sketch, "E375", {"start": v(10.1, 0.5) * mm, "end": v(10.1, 1.62) * mm});
            skLineSegment(sketch, "E376", {"start": v(10.1, 1.62) * mm, "end": v(10.6, 1.16) * mm});
            skLineSegment(sketch, "E377", {"start": v(10.6, 1.16) * mm, "end": v(10.6, 0.49) * mm});
            skLineSegment(sketch, "E378", {"start": v(8.7, 0.76) * mm, "end": v(8.7, 2.6) * mm});
            skLineSegment(sketch, "E379", {"start": v(8.7, 2.6) * mm, "end": v(7.76, 1.65) * mm});
            skLineSegment(sketch, "E380", {"start": v(7.76, 1.65) * mm, "end": v(8.7, 0.76) * mm});
            skLineSegment(sketch, "E381", {"start": v(8.7, 0.53) * mm, "end": v(7.64, 1.52) * mm});
            skLineSegment(sketch, "E382", {"start": v(7.64, 1.52) * mm, "end": v(7.64, 0.53) * mm});
            skLineSegment(sketch, "E383", {"start": v(7.64, 0.53) * mm, "end": v(8.7, 0.53) * mm});
            skLineSegment(sketch, "E384", {"start": v(9.92, 2.84) * mm, "end": v(9.92, 1.94) * mm});
            skLineSegment(sketch, "E385", {"start": v(9.92, 1.94) * mm, "end": v(9.33, 1.33) * mm});
            skLineSegment(sketch, "E386", {"start": v(9.33, 1.33) * mm, "end": v(8.87, 1.79) * mm});
            skLineSegment(sketch, "E387", {"start": v(8.87, 1.79) * mm, "end": v(9.92, 2.84) * mm});
            skLineSegment(sketch, "E388", {"start": v(9.21, 0.5) * mm, "end": v(9.21, 1.2) * mm});
            skLineSegment(sketch, "E389", {"start": v(9.21, 1.2) * mm, "end": v(8.87, 1.54) * mm});
            skLineSegment(sketch, "E390", {"start": v(8.87, 1.54) * mm, "end": v(8.87, 0.53) * mm});
            skLineSegment(sketch, "E391", {"start": v(8.87, 0.53) * mm, "end": v(9.21, 0.5) * mm});
            skLineSegment(sketch, "E392", {"start": v(9.92, 0.51) * mm, "end": v(9.38, 0.5) * mm});
            skLineSegment(sketch, "E393", {"start": v(9.38, 0.5) * mm, "end": v(9.38, 1.04) * mm});
            skLineSegment(sketch, "E394", {"start": v(9.38, 1.04) * mm, "end": v(9.92, 0.5) * mm});
            skLineSegment(sketch, "E395", {"start": v(7.46, 2.4) * mm, "end": v(7.46, 0.78) * mm});
            skLineSegment(sketch, "E396", {"start": v(7.46, 0.78) * mm, "end": v(6.76, 1.54) * mm});
            skLineSegment(sketch, "E397", {"start": v(6.76, 1.54) * mm, "end": v(7.46, 2.4) * mm});
            skLineSegment(sketch, "E398", {"start": v(-18.87, 4.05) * mm, "end": v(-20.44, 2.02) * mm});
            skLineSegment(sketch, "E399", {"start": v(-20.44, 2.02) * mm, "end": v(-20.44, 1.7) * mm});
            skLineSegment(sketch, "E400", {"start": v(-20.44, 1.7) * mm, "end": v(-19.74, 1.1) * mm});
            skLineSegment(sketch, "E401", {"start": v(-19.74, 1.1) * mm, "end": v(-18.87, 2.38) * mm});
            skLineSegment(sketch, "E402", {"start": v(-18.87, 2.38) * mm, "end": v(-18.87, 4.05) * mm});
            skLineSegment(sketch, "E403", {"start": v(-16.96, 4.96) * mm, "end": v(-16.96, 2.64) * mm});
            skLineSegment(sketch, "E404", {"start": v(-16.96, 2.64) * mm, "end": v(-18.5, 2.63) * mm});
            skLineSegment(sketch, "E405", {"start": v(-18.5, 2.63) * mm, "end": v(-16.96, 4.96) * mm});
            skLineSegment(sketch, "E406", {"start": v(-17.08, 2.48) * mm, "end": v(-18.61, 2.46) * mm});
            skLineSegment(sketch, "E407", {"start": v(-18.61, 2.46) * mm, "end": v(-18.7, 2.33) * mm});
            skLineSegment(sketch, "E408", {"start": v(-18.7, 2.33) * mm, "end": v(-18.74, 2.19) * mm});
            skLineSegment(sketch, "E409", {"start": v(-18.74, 2.19) * mm, "end": v(-17.87, 1.37) * mm});
            skLineSegment(sketch, "E410", {"start": v(-17.87, 1.37) * mm, "end": v(-17.08, 2.48) * mm});
            skLineSegment(sketch, "E411", {"start": v(-18.7, 0.23) * mm, "end": v(-18.7, 1.91) * mm});
            skLineSegment(sketch, "E412", {"start": v(-18.7, 1.91) * mm, "end": v(-17.9, 1.17) * mm});
            skLineSegment(sketch, "E413", {"start": v(-17.9, 1.17) * mm, "end": v(-17.9, 0.27) * mm});
            skLineSegment(sketch, "E414", {"start": v(-17.9, 0.27) * mm, "end": v(-18.7, 0.23) * mm});
            skLineSegment(sketch, "E415", {"start": v(-20.44, 0.15) * mm, "end": v(-20.44, 1.47) * mm});
            skLineSegment(sketch, "E416", {"start": v(-20.44, 1.47) * mm, "end": v(-19.74, 0.92) * mm});
            skLineSegment(sketch, "E417", {"start": v(-19.74, 0.92) * mm, "end": v(-19.74, 0.2) * mm});
            skLineSegment(sketch, "E418", {"start": v(-19.74, 0.2) * mm, "end": v(-20.44, 0.15) * mm});
            skLineSegment(sketch, "E419", {"start": v(-19.57, 0.78) * mm, "end": v(-19.57, 0.2) * mm});
            skLineSegment(sketch, "E420", {"start": v(-19.57, 0.2) * mm, "end": v(-18.87, 0.23) * mm});
            skLineSegment(sketch, "E421", {"start": v(-18.87, 0.23) * mm, "end": v(-19.57, 0.78) * mm});
            skLineSegment(sketch, "E422", {"start": v(-20.6, 3.13) * mm, "end": v(-22.15, 1.6) * mm});
            skLineSegment(sketch, "E423", {"start": v(-22.15, 1.6) * mm, "end": v(-21.43, 1.02) * mm});
            skLineSegment(sketch, "E424", {"start": v(-21.43, 1.02) * mm, "end": v(-20.6, 2.08) * mm});
            skLineSegment(sketch, "E425", {"start": v(-20.6, 2.08) * mm, "end": v(-20.6, 3.13) * mm});
            skLineSegment(sketch, "E426", {"start": v(-22.16, 1.39) * mm, "end": v(-22.16, 0.1) * mm});
            skLineSegment(sketch, "E427", {"start": v(-22.16, 0.1) * mm, "end": v(-21.46, 0.1) * mm});
            skLineSegment(sketch, "E428", {"start": v(-21.46, 0.1) * mm, "end": v(-21.46, 0.83) * mm});
            skLineSegment(sketch, "E429", {"start": v(-21.46, 0.83) * mm, "end": v(-22.16, 1.39) * mm});
            skLineSegment(sketch, "E430", {"start": v(-21.3, 0.7) * mm, "end": v(-21.3, 0.1) * mm});
            skLineSegment(sketch, "E431", {"start": v(-21.3, 0.1) * mm, "end": v(-20.6, 0.15) * mm});
            skLineSegment(sketch, "E432", {"start": v(-20.6, 0.15) * mm, "end": v(-21.3, 0.7) * mm});
            skLineSegment(sketch, "E433", {"start": v(-17.74, 1.01) * mm, "end": v(-17.74, 0.27) * mm});
            skLineSegment(sketch, "E434", {"start": v(-17.74, 0.27) * mm, "end": v(-16.96, 0.3) * mm});
            skLineSegment(sketch, "E435", {"start": v(-16.96, 0.3) * mm, "end": v(-17.74, 1.01) * mm});
            skLineSegment(sketch, "E436", {"start": v(-26.08, 1.6) * mm, "end": v(-26.95, 0.73) * mm});
            skLineSegment(sketch, "E437", {"start": v(-26.95, 0.73) * mm, "end": v(-26.08, 0.16) * mm});
            skLineSegment(sketch, "E438", {"start": v(-26.08, 0.16) * mm, "end": v(-26.08, 1.6) * mm});
            skLineSegment(sketch, "E439", {"start": v(-24.93, 1.81) * mm, "end": v(-25.82, 0.93) * mm});
            skLineSegment(sketch, "E440", {"start": v(-25.82, 0.93) * mm, "end": v(-24.93, 0.21) * mm});
            skLineSegment(sketch, "E441", {"start": v(-24.93, 0.21) * mm, "end": v(-24.93, 1.81) * mm});
            skLineSegment(sketch, "E442", {"start": v(-23.7, 2.17) * mm, "end": v(-24.63, 1.24) * mm});
            skLineSegment(sketch, "E443", {"start": v(-24.63, 1.24) * mm, "end": v(-24.24, 0.83) * mm});
            skLineSegment(sketch, "E444", {"start": v(-24.24, 0.83) * mm, "end": v(-23.7, 1.4) * mm});
            skLineSegment(sketch, "E445", {"start": v(-23.7, 1.4) * mm, "end": v(-23.7, 2.17) * mm});
            skLineSegment(sketch, "E446", {"start": v(-23.53, 1.32) * mm, "end": v(-23.53, 0.04) * mm});
            skLineSegment(sketch, "E447", {"start": v(-23.53, 0.04) * mm, "end": v(-23.06, 0.07) * mm});
            skLineSegment(sketch, "E448", {"start": v(-23.06, 0.07) * mm, "end": v(-23.06, 0.83) * mm});
            skLineSegment(sketch, "E449", {"start": v(-23.06, 0.83) * mm, "end": v(-23.53, 1.32) * mm});
            skLineSegment(sketch, "E450", {"start": v(-23.41, 1.44) * mm, "end": v(-22.98, 1) * mm});
            skLineSegment(sketch, "E451", {"start": v(-22.98, 1) * mm, "end": v(-22.33, 1.65) * mm});
            skLineSegment(sketch, "E452", {"start": v(-22.33, 1.65) * mm, "end": v(-22.33, 2.58) * mm});
            skLineSegment(sketch, "E453", {"start": v(-22.33, 2.58) * mm, "end": v(-23.41, 1.44) * mm});
            skLineSegment(sketch, "E454", {"start": v(-22.89, 0.66) * mm, "end": v(-22.89, 0.07) * mm});
            skLineSegment(sketch, "E455", {"start": v(-22.89, 0.07) * mm, "end": v(-22.33, 0.1) * mm});
            skLineSegment(sketch, "E456", {"start": v(-22.33, 0.1) * mm, "end": v(-22.89, 0.66) * mm});
            skLineSegment(sketch, "E457", {"start": v(-24.76, -0.01) * mm, "end": v(-24.76, 1.12) * mm});
            skLineSegment(sketch, "E458", {"start": v(-24.76, 1.12) * mm, "end": v(-24.3, 0.65) * mm});
            skLineSegment(sketch, "E459", {"start": v(-24.3, 0.65) * mm, "end": v(-24.3, 0.01) * mm});
            skLineSegment(sketch, "E460", {"start": v(-24.3, 0.01) * mm, "end": v(-24.76, -0.01) * mm});
            skLineSegment(sketch, "E461", {"start": v(-24.13, 0.47) * mm, "end": v(-24.13, 0.01) * mm});
            skLineSegment(sketch, "E462", {"start": v(-24.13, 0.01) * mm, "end": v(-23.7, 0.04) * mm});
            skLineSegment(sketch, "E463", {"start": v(-23.7, 0.04) * mm, "end": v(-24.13, 0.47) * mm});
            skLineSegment(sketch, "E464", {"start": v(-25.9, 0.78) * mm, "end": v(-25.9, -0.04) * mm});
            skLineSegment(sketch, "E465", {"start": v(-25.9, -0.04) * mm, "end": v(-24.93, -0.01) * mm});
            skLineSegment(sketch, "E466", {"start": v(-24.93, -0.01) * mm, "end": v(-25.9, 0.78) * mm});
            skLineSegment(sketch, "E467", {"start": v(-27.05, 0.6) * mm, "end": v(-27.05, -0.14) * mm});
            skLineSegment(sketch, "E468", {"start": v(-27.05, -0.14) * mm, "end": v(-26.08, -0.04) * mm});
            skLineSegment(sketch, "E469", {"start": v(-26.08, -0.04) * mm, "end": v(-27.05, 0.6) * mm});
            skLineSegment(sketch, "E470", {"start": v(-27.22, 1.34) * mm, "end": v(-27.84, 0.72) * mm});
            skLineSegment(sketch, "E471", {"start": v(-27.84, 0.72) * mm, "end": v(-27.22, 0.1) * mm});
            skLineSegment(sketch, "E472", {"start": v(-27.22, 0.1) * mm, "end": v(-27.22, 1.34) * mm});
            skLineSegment(sketch, "E473", {"start": v(-27.92, 0.56) * mm, "end": v(-27.92, -0.17) * mm});
            skLineSegment(sketch, "E474", {"start": v(-27.92, -0.17) * mm, "end": v(-27.23, -0.14) * mm});
            skLineSegment(sketch, "E475", {"start": v(-27.23, -0.14) * mm, "end": v(-27.92, 0.56) * mm});
            skLineSegment(sketch, "E476", {"start": v(-28.1, 0.03) * mm, "end": v(-28.1, 1.2) * mm});
            skLineSegment(sketch, "E477", {"start": v(-28.1, 1.2) * mm, "end": v(-28.83, 0.45) * mm});
            skLineSegment(sketch, "E478", {"start": v(-28.83, 0.45) * mm, "end": v(-28.1, 0.03) * mm});
            skLineSegment(sketch, "E479", {"start": v(-28.96, 0.33) * mm, "end": v(-29.53, -0.24) * mm});
            skLineSegment(sketch, "E480", {"start": v(-29.53, -0.24) * mm, "end": v(-28.1, -0.17) * mm});
            skLineSegment(sketch, "E481", {"start": v(-28.1, -0.17) * mm, "end": v(-28.96, 0.33) * mm});
            skLineSegment(sketch, "E482", {"start": v(-16.8, 4.97) * mm, "end": v(-16.8, 2.63) * mm});
            skLineSegment(sketch, "E483", {"start": v(-16.8, 2.63) * mm, "end": v(-15.13, 2.65) * mm});
            skLineSegment(sketch, "E484", {"start": v(-15.13, 2.65) * mm, "end": v(-16.8, 4.97) * mm});
            skLineSegment(sketch, "E485", {"start": v(-16.64, 2.46) * mm, "end": v(-15.83, 1.57) * mm});
            skLineSegment(sketch, "E486", {"start": v(-15.83, 1.57) * mm, "end": v(-15, 2.46) * mm});
            skLineSegment(sketch, "E487", {"start": v(-15, 2.46) * mm, "end": v(-15, 2.48) * mm});
            skLineSegment(sketch, "E488", {"start": v(-15, 2.48) * mm, "end": v(-16.64, 2.46) * mm});
            skLineSegment(sketch, "E489", {"start": v(-14.8, 4.1) * mm, "end": v(-14.8, 2.5) * mm});
            skLineSegment(sketch, "E490", {"start": v(-14.8, 2.5) * mm, "end": v(-14, 1.37) * mm});
            skLineSegment(sketch, "E491", {"start": v(-14, 1.37) * mm, "end": v(-13.22, 2.14) * mm});
            skLineSegment(sketch, "E492", {"start": v(-13.22, 2.14) * mm, "end": v(-13.22, 2.26) * mm});
            skLineSegment(sketch, "E493", {"start": v(-13.22, 2.26) * mm, "end": v(-14.8, 4.1) * mm});
            skLineSegment(sketch, "E494", {"start": v(-13.96, 0.4) * mm, "end": v(-13.96, 1.17) * mm});
            skLineSegment(sketch, "E495", {"start": v(-13.96, 1.17) * mm, "end": v(-13.22, 1.9) * mm});
            skLineSegment(sketch, "E496", {"start": v(-13.22, 1.9) * mm, "end": v(-13.22, 0.48) * mm});
            skLineSegment(sketch, "E497", {"start": v(-13.22, 0.48) * mm, "end": v(-13.96, 0.4) * mm});
            skLineSegment(sketch, "E498", {"start": v(-14.98, 2.23) * mm, "end": v(-15.76, 1.4) * mm});
            skLineSegment(sketch, "E499", {"start": v(-15.76, 1.4) * mm, "end": v(-15.76, 0.33) * mm});
            skLineSegment(sketch, "E500", {"start": v(-15.76, 0.33) * mm, "end": v(-14.98, 0.35) * mm});
            skLineSegment(sketch, "E501", {"start": v(-14.98, 0.35) * mm, "end": v(-14.98, 2.23) * mm});
            skLineSegment(sketch, "E502", {"start": v(-15.93, 1.21) * mm, "end": v(-16.8, 0.3) * mm});
            skLineSegment(sketch, "E503", {"start": v(-16.8, 0.3) * mm, "end": v(-15.93, 0.33) * mm});
            skLineSegment(sketch, "E504", {"start": v(-15.93, 0.33) * mm, "end": v(-15.93, 1.21) * mm});
            skLineSegment(sketch, "E505", {"start": v(-14.13, 1) * mm, "end": v(-14.8, 0.35) * mm});
            skLineSegment(sketch, "E506", {"start": v(-14.8, 0.35) * mm, "end": v(-14.13, 0.4) * mm});
            skLineSegment(sketch, "E507", {"start": v(-14.13, 0.4) * mm, "end": v(-14.13, 1) * mm});
            skLineSegment(sketch, "E508", {"start": v(-13.05, 3.62) * mm, "end": v(-13.05, 2.33) * mm});
            skLineSegment(sketch, "E509", {"start": v(-13.05, 2.33) * mm, "end": v(-12.24, 1.4) * mm});
            skLineSegment(sketch, "E510", {"start": v(-12.24, 1.4) * mm, "end": v(-11.54, 2) * mm});
            skLineSegment(sketch, "E511", {"start": v(-11.54, 2) * mm, "end": v(-13.05, 3.62) * mm});
            skLineSegment(sketch, "E512", {"start": v(-11.35, 3.13) * mm, "end": v(-11.35, 2.06) * mm});
            skLineSegment(sketch, "E513", {"start": v(-11.35, 2.06) * mm, "end": v(-10.68, 1.33) * mm});
            skLineSegment(sketch, "E514", {"start": v(-10.68, 1.33) * mm, "end": v(-10.12, 1.86) * mm});
            skLineSegment(sketch, "E515", {"start": v(-10.12, 1.86) * mm, "end": v(-11.35, 3.13) * mm});
            skLineSegment(sketch, "E516", {"start": v(-11.53, 1.78) * mm, "end": v(-12.13, 1.27) * mm});
            skLineSegment(sketch, "E517", {"start": v(-12.13, 1.27) * mm, "end": v(-12.13, 0.46) * mm});
            skLineSegment(sketch, "E518", {"start": v(-12.13, 0.46) * mm, "end": v(-11.53, 0.48) * mm});
            skLineSegment(sketch, "E519", {"start": v(-11.53, 0.48) * mm, "end": v(-11.53, 1.78) * mm});
            skLineSegment(sketch, "E520", {"start": v(-12.3, 1.12) * mm, "end": v(-13.05, 0.48) * mm});
            skLineSegment(sketch, "E521", {"start": v(-13.05, 0.48) * mm, "end": v(-12.3, 0.46) * mm});
            skLineSegment(sketch, "E522", {"start": v(-12.3, 0.46) * mm, "end": v(-12.3, 1.12) * mm});
            skLineSegment(sketch, "E523", {"start": v(-11.35, 0.48) * mm, "end": v(-10.8, 1) * mm});
            skLineSegment(sketch, "E524", {"start": v(-10.8, 1) * mm, "end": v(-10.8, 0.49) * mm});
            skLineSegment(sketch, "E525", {"start": v(-10.8, 0.49) * mm, "end": v(-11.35, 0.48) * mm});
            skLineSegment(sketch, "E526", {"start": v(-10.62, 0.49) * mm, "end": v(-10.12, 0.5) * mm});
            skLineSegment(sketch, "E527", {"start": v(-10.12, 0.5) * mm, "end": v(-10.12, 1.62) * mm});
            skLineSegment(sketch, "E528", {"start": v(-10.12, 1.62) * mm, "end": v(-10.62, 1.16) * mm});
            skLineSegment(sketch, "E529", {"start": v(-10.62, 1.16) * mm, "end": v(-10.62, 0.49) * mm});
            skLineSegment(sketch, "E530", {"start": v(-8.72, 0.76) * mm, "end": v(-8.72, 2.6) * mm});
            skLineSegment(sketch, "E531", {"start": v(-8.72, 2.6) * mm, "end": v(-7.78, 1.65) * mm});
            skLineSegment(sketch, "E532", {"start": v(-7.78, 1.65) * mm, "end": v(-8.72, 0.76) * mm});
            skLineSegment(sketch, "E533", {"start": v(-8.72, 0.53) * mm, "end": v(-7.66, 1.52) * mm});
            skLineSegment(sketch, "E534", {"start": v(-7.66, 1.52) * mm, "end": v(-7.66, 0.53) * mm});
            skLineSegment(sketch, "E535", {"start": v(-7.66, 0.53) * mm, "end": v(-8.72, 0.53) * mm});
            skLineSegment(sketch, "E536", {"start": v(-9.95, 2.84) * mm, "end": v(-9.95, 1.94) * mm});
            skLineSegment(sketch, "E537", {"start": v(-9.95, 1.94) * mm, "end": v(-9.36, 1.33) * mm});
            skLineSegment(sketch, "E538", {"start": v(-9.36, 1.33) * mm, "end": v(-8.9, 1.79) * mm});
            skLineSegment(sketch, "E539", {"start": v(-8.9, 1.79) * mm, "end": v(-9.95, 2.84) * mm});
            skLineSegment(sketch, "E540", {"start": v(-9.24, 0.5) * mm, "end": v(-9.24, 1.2) * mm});
            skLineSegment(sketch, "E541", {"start": v(-9.24, 1.2) * mm, "end": v(-8.9, 1.54) * mm});
            skLineSegment(sketch, "E542", {"start": v(-8.9, 1.54) * mm, "end": v(-8.9, 0.53) * mm});
            skLineSegment(sketch, "E543", {"start": v(-8.9, 0.53) * mm, "end": v(-9.24, 0.5) * mm});
            skLineSegment(sketch, "E544", {"start": v(-9.95, 0.51) * mm, "end": v(-9.41, 0.5) * mm});
            skLineSegment(sketch, "E545", {"start": v(-9.41, 0.5) * mm, "end": v(-9.41, 1.04) * mm});
            skLineSegment(sketch, "E546", {"start": v(-9.41, 1.04) * mm, "end": v(-9.95, 0.5) * mm});
            skLineSegment(sketch, "E547", {"start": v(-7.5, 2.4) * mm, "end": v(-7.5, 0.78) * mm});
            skLineSegment(sketch, "E548", {"start": v(-7.5, 0.78) * mm, "end": v(-6.78, 1.54) * mm});
            skLineSegment(sketch, "E549", {"start": v(-6.78, 1.54) * mm, "end": v(-7.5, 2.4) * mm});
            skLineSegment(sketch, "E550", {"start": v(-29.53, -0.24) * mm, "end": v(-29.65, -0.12) * mm});
            skLineSegment(sketch, "E551", {"start": v(-29.65, -0.12) * mm, "end": v(-29.08, 0.45) * mm});
            skLineSegment(sketch, "E552", {"start": v(-29.53, -0.25) * mm, "end": v(-29.65, -0.12) * mm});
            skLineSegment(sketch, "E553", {"start": v(-29.65, -0.12) * mm, "end": v(-28.1, 1.44) * mm});
            skLineSegment(sketch, "E554", {"start": v(-28.1, 1.44) * mm, "end": v(-27.22, 1.58) * mm});
            skLineSegment(sketch, "E555", {"start": v(-27.22, 1.58) * mm, "end": v(-26.08, 1.84) * mm});
            skLineSegment(sketch, "E556", {"start": v(-26.08, 1.84) * mm, "end": v(-24.93, 2.05) * mm});
            skLineSegment(sketch, "E557", {"start": v(-24.93, 2.05) * mm, "end": v(-23.7, 2.4) * mm});
            skLineSegment(sketch, "E558", {"start": v(-23.7, 2.4) * mm, "end": v(-22.33, 2.83) * mm});
            skLineSegment(sketch, "E559", {"start": v(-22.33, 2.83) * mm, "end": v(-20.6, 3.38) * mm});
            skLineSegment(sketch, "E560", {"start": v(-20.6, 3.38) * mm, "end": v(-18.87, 4.33) * mm});
            skLineSegment(sketch, "E561", {"start": v(-18.87, 4.33) * mm, "end": v(-16.96, 5.27) * mm});
            skLineSegment(sketch, "E562", {"start": v(-16.96, 5.27) * mm, "end": v(-16.8, 5.27) * mm});
            skLineSegment(sketch, "E563", {"start": v(-16.8, 5.27) * mm, "end": v(-14.8, 4.37) * mm});
            skLineSegment(sketch, "E564", {"start": v(-14.8, 4.37) * mm, "end": v(-13.05, 3.88) * mm});
            skLineSegment(sketch, "E565", {"start": v(-13.05, 3.88) * mm, "end": v(-11.35, 3.38) * mm});
            skLineSegment(sketch, "E566", {"start": v(-11.35, 3.38) * mm, "end": v(-9.95, 3.09) * mm});
            skLineSegment(sketch, "E567", {"start": v(-9.95, 3.09) * mm, "end": v(-8.72, 2.85) * mm});
            skLineSegment(sketch, "E568", {"start": v(-8.72, 2.85) * mm, "end": v(-7.5, 2.66) * mm});
            skLineSegment(sketch, "E569", {"start": v(-7.5, 2.66) * mm, "end": v(-6.64, 2.53) * mm});
            skLineSegment(sketch, "E570", {"start": v(-6.64, 2.53) * mm, "end": v(-5.77, 2.45) * mm});
            skLineSegment(sketch, "E571", {"start": v(-5.77, 2.45) * mm, "end": v(-4.14, 2.36) * mm});
            skLineSegment(sketch, "E572", {"start": v(-4.14, 2.36) * mm, "end": v(-2.41, 2.27) * mm});
            skLineSegment(sketch, "E573", {"start": v(-2.41, 2.27) * mm, "end": v(-0.98, 2.28) * mm});
            skLineSegment(sketch, "E574", {"start": v(-0.98, 2.28) * mm, "end": v(0.72, 2.28) * mm});
            skLineSegment(sketch, "E575", {"start": v(0.72, 2.28) * mm, "end": v(2.38, 2.28) * mm});
            skLineSegment(sketch, "E576", {"start": v(8.67, 2.82) * mm, "end": v(9.92, 3.09) * mm});
            skLineSegment(sketch, "E577", {"start": v(9.92, 3.09) * mm, "end": v(11.33, 3.38) * mm});
            skLineSegment(sketch, "E578", {"start": v(11.33, 3.38) * mm, "end": v(13.02, 3.88) * mm});
            skLineSegment(sketch, "E579", {"start": v(13.02, 3.88) * mm, "end": v(14.78, 4.37) * mm});
            skLineSegment(sketch, "E580", {"start": v(14.78, 4.37) * mm, "end": v(16.77, 5.27) * mm});
            skLineSegment(sketch, "E581", {"start": v(16.77, 5.27) * mm, "end": v(17.01, 5.27) * mm});
            skLineSegment(sketch, "E582", {"start": v(17.01, 5.27) * mm, "end": v(18.84, 4.33) * mm});
            skLineSegment(sketch, "E583", {"start": v(18.84, 4.33) * mm, "end": v(20.58, 3.38) * mm});
            skLineSegment(sketch, "E584", {"start": v(24.9, 2.05) * mm, "end": v(26.05, 1.84) * mm});
            skLineSegment(sketch, "E585", {"start": v(26.05, 1.84) * mm, "end": v(27.2, 1.58) * mm});
            skLineSegment(sketch, "E586", {"start": v(27.2, 1.58) * mm, "end": v(28.06, 1.44) * mm});
            skLineSegment(sketch, "E587", {"start": v(28.06, 1.44) * mm, "end": v(29.05, 0.45) * mm});
            skLineSegment(sketch, "E588", {"start": v(29.05, 0.45) * mm, "end": v(29.62, -0.12) * mm});
            skLineSegment(sketch, "E589", {"start": v(29.62, -0.12) * mm, "end": v(29.5, -0.24) * mm});
            skLineSegment(sketch, "E590", {"start": v(30.1, -0.5) * mm, "end": v(28.06, 1.44) * mm});
            skLineSegment(sketch, "E591", {"start": v(28.06, 1.44) * mm, "end": v(27.2, 1.58) * mm});
            skLineSegment(sketch, "E592", {"start": v(27.2, 1.58) * mm, "end": v(26.05, 1.84) * mm});
            skLineSegment(sketch, "E593", {"start": v(26.05, 1.84) * mm, "end": v(24.9, 2.05) * mm});
            skLineSegment(sketch, "E594", {"start": v(24.9, 2.05) * mm, "end": v(20.58, 3.38) * mm});
            skLineSegment(sketch, "E595", {"start": v(20.58, 3.38) * mm, "end": v(16.94, 5.27) * mm});
            skLineSegment(sketch, "E596", {"start": v(16.94, 5.27) * mm, "end": v(16.77, 5.27) * mm});
            skLineSegment(sketch, "E597", {"start": v(16.77, 5.27) * mm, "end": v(14.78, 4.37) * mm});
            skLineSegment(sketch, "E598", {"start": v(14.78, 4.37) * mm, "end": v(11.33, 3.38) * mm});
            skLineSegment(sketch, "E599", {"start": v(11.33, 3.38) * mm, "end": v(8.7, 2.85) * mm});
            skLineSegment(sketch, "E600", {"start": v(8.7, 2.85) * mm, "end": v(7.46, 2.66) * mm});
            skLineSegment(sketch, "E601", {"start": v(7.46, 2.66) * mm, "end": v(5.74, 2.45) * mm});
            skLineSegment(sketch, "E602", {"start": v(5.74, 2.45) * mm, "end": v(2.38, 2.28) * mm});
            skLineSegment(sketch, "E603", {"start": v(2.38, 2.28) * mm, "end": v(-0.8, 2.28) * mm});
            skLineSegment(sketch, "E604", {"start": v(-0.8, 2.28) * mm, "end": v(-2.4, 2.28) * mm});
            skLineSegment(sketch, "E605", {"start": v(-2.4, 2.28) * mm, "end": v(-5.77, 2.45) * mm});
            skLineSegment(sketch, "E606", {"start": v(-5.77, 2.45) * mm, "end": v(-7.5, 2.66) * mm});
            skLineSegment(sketch, "E607", {"start": v(-7.5, 2.66) * mm, "end": v(-11.34, 3.37) * mm});
            skLineSegment(sketch, "E608", {"start": v(-11.34, 3.37) * mm, "end": v(-14.8, 4.37) * mm});
            skLineSegment(sketch, "E609", {"start": v(-14.8, 4.37) * mm, "end": v(-16.8, 5.27) * mm});
            skLineSegment(sketch, "E610", {"start": v(-16.8, 5.27) * mm, "end": v(-16.96, 5.27) * mm});
            skLineSegment(sketch, "E611", {"start": v(-16.96, 5.27) * mm, "end": v(-18.87, 4.33) * mm});
            skLineSegment(sketch, "E612", {"start": v(-18.87, 4.33) * mm, "end": v(-20.6, 3.38) * mm});
            skLineSegment(sketch, "E613", {"start": v(-20.6, 3.38) * mm, "end": v(-23.7, 2.4) * mm});
            skLineSegment(sketch, "E614", {"start": v(-23.7, 2.4) * mm, "end": v(-24.93, 2.05) * mm});
            skLineSegment(sketch, "E615", {"start": v(-24.93, 2.05) * mm, "end": v(-27.22, 1.58) * mm});
            skLineSegment(sketch, "E616", {"start": v(-27.22, 1.58) * mm, "end": v(-28.1, 1.44) * mm});
            skLineSegment(sketch, "E617", {"start": v(-28.1, 1.44) * mm, "end": v(-30.11, -0.52) * mm});
            skLineSegment(sketch, "E618", {"start": v(-16.96, 5.27) * mm, "end": v(-16.89, 5.64) * mm});
            skLineSegment(sketch, "E619", {"start": v(-16.89, 5.64) * mm, "end": v(-16.8, 5.27) * mm});
            skLineSegment(sketch, "E620", {"start": v(16.77, 5.27) * mm, "end": v(16.84, 5.64) * mm});
            skLineSegment(sketch, "E621", {"start": v(16.84, 5.64) * mm, "end": v(16.94, 5.27) * mm});
            skLineSegment(sketch, "E622", {"start": v(-30.11, -0.52) * mm, "end": v(-29.27, -0.5) * mm});
            skLineSegment(sketch, "E623", {"start": v(-29.27, -0.5) * mm, "end": v(-27.83, -0.42) * mm});
            skLineSegment(sketch, "E624", {"start": v(-27.83, -0.42) * mm, "end": v(-21.9, -0.16) * mm});
            skLineSegment(sketch, "E625", {"start": v(-21.9, -0.16) * mm, "end": v(-16.53, 0.04) * mm});
            skLineSegment(sketch, "E626", {"start": v(-16.53, 0.04) * mm, "end": v(-5.68, 0.28) * mm});
            skLineSegment(sketch, "E627", {"start": v(-5.68, 0.28) * mm, "end": v(-0.72, 0.3) * mm});
            skLineSegment(sketch, "E628", {"start": v(-0.72, 0.3) * mm, "end": v(9.65, 0.26) * mm});
            skLineSegment(sketch, "E629", {"start": v(9.65, 0.26) * mm, "end": v(8.3, 0.26) * mm});
            skLineSegment(sketch, "E630", {"start": v(8.3, 0.26) * mm, "end": v(18.14, 0.02) * mm});
            skLineSegment(sketch, "E631", {"start": v(18.14, 0.02) * mm, "end": v(25.17, -0.26) * mm});
            skLineSegment(sketch, "E632", {"start": v(25.17, -0.26) * mm, "end": v(29.76, -0.5) * mm});
            skLineSegment(sketch, "E633", {"start": v(29.76, -0.5) * mm, "end": v(30.1, -0.5) * mm});
            skLineSegment(sketch, "E634", {"start": v(-4.94, 1.36) * mm, "end": v(-5.77, 0.53) * mm});
            skLineSegment(sketch, "E635", {"start": v(-4.14, 0.55) * mm, "end": v(-4.94, 1.36) * mm});
            skLineSegment(sketch, "E636", {"start": v(-30.11, -0.52) * mm, "end": v(-30.17, -3.73) * mm, "construction": true});
            skLineSegment(sketch, "E637.bottom", {"start": v(-30.11, -0.52) * mm, "end": v(30.17, -0.52) * mm, "construction": true});
            skLineSegment(sketch, "E637.top", {"start": v(-30.11, -3.47) * mm, "end": v(30.17, -3.47) * mm, "construction": true});
            skLineSegment(sketch, "E637.left", {"start": v(-30.11, -0.52) * mm, "end": v(-30.11, -3.47) * mm, "construction": true});
            skLineSegment(sketch, "E637.right", {"start": v(30.17, -0.52) * mm, "end": v(30.17, -3.47) * mm, "construction": true});
            skLineSegment(sketch, "E638", {"start": v(-30.11, -2) * mm, "end": v(30.14, -2) * mm, "construction": true});
            skLineSegment(sketch, "E639.bottom", {"start": v(-30.11, -2) * mm, "end": v(30.12, -2) * mm});
            skLineSegment(sketch, "E639.top", {"start": v(-30.11, -6.75) * mm, "end": v(30.12, -6.75) * mm});
            skLineSegment(sketch, "E639.left", {"start": v(-30.11, -2) * mm, "end": v(-30.11, -6.75) * mm});
            skLineSegment(sketch, "E639.right", {"start": v(30.12, -2) * mm, "end": v(30.12, -6.75) * mm});
            skLineSegment(sketch, "E640.bottom", {"start": v(-29, -1.2) * mm, "end": v(29, -1.2) * mm});
            skLineSegment(sketch, "E640.top", {"start": v(-29, -2.8) * mm, "end": v(29, -2.8) * mm});
            skLineSegment(sketch, "E640.left", {"start": v(-29, -1.2) * mm, "end": v(-29, -2.8) * mm});
            skLineSegment(sketch, "E640.right", {"start": v(29, -1.2) * mm, "end": v(29, -2.8) * mm});
            skPoint(sketch, "E641", {"position": v(0, -2) * mm});
            skPoint(sketch, "E642", {"position": v(0.03, -3.47) * mm});
            skPoint(sketch, "E643", {"position": v(0, -0.52) * mm});
            skPoint(sketch, "E643.positionSnap0", {"position": v(0.03, -0.52) * mm});
            skLineSegment(sketch, "E644", {"start": v(-29, -1.2) * mm, "end": v(29, -2.8) * mm, "construction": true});
            skPoint(sketch, "E645", {"position": v(0, -1.2) * mm});
            skLineSegment(sketch, "E646", {"start": v(-28.91, -0.44) * mm, "end": v(30.1, -0.5) * mm});
            skSolve(sketch);
        }
        {
            var Q0;
            {var subQ12=sQuery(id+"F0.wireOp",EDGE,"E6");Q0=makeQuery(id+"F0.imprint","IMPRINT",FACE,{"disambiguationData":[TD([[makeQuery(id+"F0.imprint","IMPRINT",EDGE,{"derivedFrom":subQ12}),-1.0]])]});}
            var Q1;
            Q1=makeQuery(id+"F0.imprint","IMPRINT",FACE,{"disambiguationData":[TD([[makeQuery(id+"F0.imprint","IMPRINT",EDGE,{"derivedFrom":sQuery(id+"F0.wireOp",EDGE,"E610")}),-1.0]])]});
            var Q2;
            Q2=makeQuery(id+"F0.imprint","IMPRINT",FACE,{"disambiguationData":[TD([[makeQuery(id+"F0.imprint","IMPRINT",EDGE,{"derivedFrom":sQuery(id+"F0.wireOp",EDGE,"E596")}),-1.0]])]});
            var Q3;
            {var subQ7=sQuery(id+"F0.wireOp",EDGE,"E646");var subQ9=sQuery(id+"F0.wireOp",EDGE,"E1");var subQ10=makeQuery(id+"F0.imprint","INTERSECT",VERTEX,{"derivedFrom":[subQ9,subQ7]});Q3=makeQuery(id+"F0.imprint","IMPRINT",FACE,{"disambiguationData":[TD([[makeQuery(id+"F0.imprint","IMPRINT",EDGE,{"disambiguationData":[TD([[subQ10,-1.0]])],"derivedFrom":subQ9}),1.0]])]});}
            var Q4;
            {var subQ1=sQuery(id+"F0.wireOp",EDGE,"E7");Q4=makeQuery(id+"F0.imprint","IMPRINT",FACE,{"disambiguationData":[TD([[makeQuery(id+"F0.imprint","IMPRINT",EDGE,{"derivedFrom":subQ1}),1.0]])]});}
            var Q5;
            {var subQ0=sQuery(id+"F0.wireOp",EDGE,"E646");var subQ1=sQuery(id+"F0.wireOp",EDGE,"E9");var subQ2=makeQuery(id+"F0.imprint","INTERSECT",VERTEX,{"derivedFrom":[subQ1,subQ0]});Q5=makeQuery(id+"F0.imprint","IMPRINT",FACE,{"disambiguationData":[TD([[makeQuery(id+"F0.imprint","IMPRINT",EDGE,{"disambiguationData":[TD([[subQ2,-1.0]])],"derivedFrom":subQ1}),-1.0]])]});}
            var Q6;
            {var subQ0=sQuery(id+"F0.wireOp",EDGE,"E13");Q6=makeQuery(id+"F0.imprint","IMPRINT",FACE,{"disambiguationData":[TD([[makeQuery(id+"F0.imprint","IMPRINT",EDGE,{"derivedFrom":subQ0}),1.0]])]});}
            var Q7;
            {var subQ0=sQuery(id+"F0.wireOp",EDGE,"E632");var subQ1=sQuery(id+"F0.wireOp",EDGE,"E15");var subQ2=makeQuery(id+"F0.imprint","INTERSECT",VERTEX,{"derivedFrom":[subQ1,subQ0]});Q7=makeQuery(id+"F0.imprint","IMPRINT",FACE,{"disambiguationData":[TD([[makeQuery(id+"F0.imprint","IMPRINT",EDGE,{"disambiguationData":[TD([[subQ2,-1.0]])],"derivedFrom":subQ1}),1.0]])]});}
            var Q8;
            {var subQ0=sQuery(id+"F0.wireOp",EDGE,"E2");var subQ1=sQuery(id+"F0.wireOp",EDGE,"E1");var subQ2=makeQuery(id+"F0.imprint","INTERSECT",VERTEX,{"derivedFrom":[subQ1,subQ0]});Q8=makeQuery(id+"F0.imprint","IMPRINT",FACE,{"disambiguationData":[TD([[makeQuery(id+"F0.imprint","IMPRINT",EDGE,{"disambiguationData":[TD([[subQ2,1.0]])],"derivedFrom":subQ1}),1.0]])]});}
            extrude(context, id + "F1", {"entities" : qUnion([Q0, Q1, Q2, Q3, Q4, Q5, Q6, Q7, Q8]), "depth" : 3 * mm, "offsetDistance" : 25.4 * mm});
        }
        {
            var Q0;
            {var subQ0=sQuery(id+"F0.wireOp",EDGE,"E13");Q0=makeQuery(id+"F0.imprint","IMPRINT",FACE,{"disambiguationData":[TD([[makeQuery(id+"F0.imprint","IMPRINT",EDGE,{"derivedFrom":subQ0}),1.0]])]});}
            var Q1;
            {var subQ3=sQuery(id+"F0.wireOp",EDGE,"E12");var subQ7=sQuery(id+"F0.wireOp",EDGE,"E15");var subQ8=makeQuery(id+"F0.imprint","INTERSECT",VERTEX,{"derivedFrom":[subQ3,subQ7]});Q1=makeQuery(id+"F0.imprint","IMPRINT",FACE,{"disambiguationData":[TD([[makeQuery(id+"F0.imprint","IMPRINT",EDGE,{"disambiguationData":[TD([[subQ8,-1.0]])],"derivedFrom":subQ3}),1.0]])]});}
            var Q2;
            {var subQ0=sQuery(id+"F0.wireOp",EDGE,"E646");var subQ1=sQuery(id+"F0.wireOp",EDGE,"E11");var subQ2=makeQuery(id+"F0.imprint","INTERSECT",VERTEX,{"derivedFrom":[subQ1,subQ0]});Q2=makeQuery(id+"F0.imprint","IMPRINT",FACE,{"disambiguationData":[TD([[makeQuery(id+"F0.imprint","IMPRINT",EDGE,{"disambiguationData":[TD([[subQ2,-1.0]])],"derivedFrom":subQ1}),1.0]])]});}
            var Q3;
            {var subQ5=sQuery(id+"F0.wireOp",EDGE,"E0");Q3=makeQuery(id+"F0.imprint","IMPRINT",FACE,{"disambiguationData":[TD([[makeQuery(id+"F0.imprint","IMPRINT",EDGE,{"derivedFrom":subQ5}),-1.0]])]});}
            var Q4;
            {var subQ0=sQuery(id+"F0.wireOp",EDGE,"E640.bottom");var subQ1=sQuery(id+"F0.wireOp",EDGE,"E9");var subQ2=makeQuery(id+"F0.imprint","INTERSECT",VERTEX,{"derivedFrom":[subQ1,subQ0]});Q4=makeQuery(id+"F0.imprint","IMPRINT",FACE,{"disambiguationData":[TD([[makeQuery(id+"F0.imprint","IMPRINT",EDGE,{"disambiguationData":[TD([[subQ2,-1.0]])],"derivedFrom":subQ1}),-1.0]])]});}
            var Q5;
            {var subQ0=sQuery(id+"F0.wireOp",EDGE,"E8");Q5=makeQuery(id+"F0.imprint","IMPRINT",FACE,{"disambiguationData":[TD([[makeQuery(id+"F0.imprint","IMPRINT",EDGE,{"derivedFrom":subQ0}),-1.0]])]});}
            var Q6;
            {var subQ0=sQuery(id+"F0.wireOp",EDGE,"E640.bottom");var subQ1=sQuery(id+"F0.wireOp",EDGE,"E1");var subQ2=makeQuery(id+"F0.imprint","INTERSECT",VERTEX,{"derivedFrom":[subQ1,subQ0]});Q6=makeQuery(id+"F0.imprint","IMPRINT",FACE,{"disambiguationData":[TD([[makeQuery(id+"F0.imprint","IMPRINT",EDGE,{"disambiguationData":[TD([[subQ2,-1.0]])],"derivedFrom":subQ1}),-1.0]])]});}
            var Q7;
            {var subQ0=sQuery(id+"F0.wireOp",EDGE,"E640.bottom");var subQ1=sQuery(id+"F0.wireOp",EDGE,"E1");var subQ2=makeQuery(id+"F0.imprint","INTERSECT",VERTEX,{"derivedFrom":[subQ1,subQ0]});Q7=makeQuery(id+"F0.imprint","IMPRINT",FACE,{"disambiguationData":[TD([[makeQuery(id+"F0.imprint","IMPRINT",EDGE,{"disambiguationData":[TD([[subQ2,-1.0]])],"derivedFrom":subQ1}),1.0]])]});}
            var Q8;
            {var subQ0=sQuery(id+"F0.wireOp",EDGE,"E0");Q8=makeQuery(id+"F0.imprint","IMPRINT",FACE,{"disambiguationData":[TD([[makeQuery(id+"F0.imprint","IMPRINT",EDGE,{"derivedFrom":subQ0}),1.0]])]});}
            var Q9;
            {var subQ1=sQuery(id+"F0.wireOp",EDGE,"E3");var subQ7=sQuery(id+"F0.wireOp",EDGE,"E646");var subQ9=makeQuery(id+"F0.imprint","INTERSECT",VERTEX,{"derivedFrom":[subQ1,subQ7]});Q9=makeQuery(id+"F0.imprint","IMPRINT",FACE,{"disambiguationData":[TD([[makeQuery(id+"F0.imprint","IMPRINT",EDGE,{"disambiguationData":[TD([[subQ9,-1.0]])],"derivedFrom":subQ1}),-1.0]])]});}
            var Q10;
            {var subQ1=sQuery(id+"F0.wireOp",EDGE,"E7");Q10=makeQuery(id+"F0.imprint","IMPRINT",FACE,{"disambiguationData":[TD([[makeQuery(id+"F0.imprint","IMPRINT",EDGE,{"derivedFrom":subQ1}),1.0]])]});}
            var Q11;
            {var subQ3=sQuery(id+"F0.wireOp",EDGE,"E4");var subQ8=sQuery(id+"F0.wireOp",EDGE,"E5");var subQ11=makeQuery(id+"F0.imprint","INTERSECT",VERTEX,{"derivedFrom":[subQ3,subQ8]});Q11=makeQuery(id+"F0.imprint","IMPRINT",FACE,{"disambiguationData":[TD([[makeQuery(id+"F0.imprint","IMPRINT",EDGE,{"disambiguationData":[TD([[subQ11,1.0]])],"derivedFrom":subQ3}),1.0]])]});}
            extrude(context, id + "F2", {"entities" : qUnion([Q0, Q1, Q2, Q3, Q4, Q5, Q6, Q7, Q8, Q9, Q10, Q11]), "depth" : 6 * mm, "offsetDistance" : 25 * mm});
        }
    });
